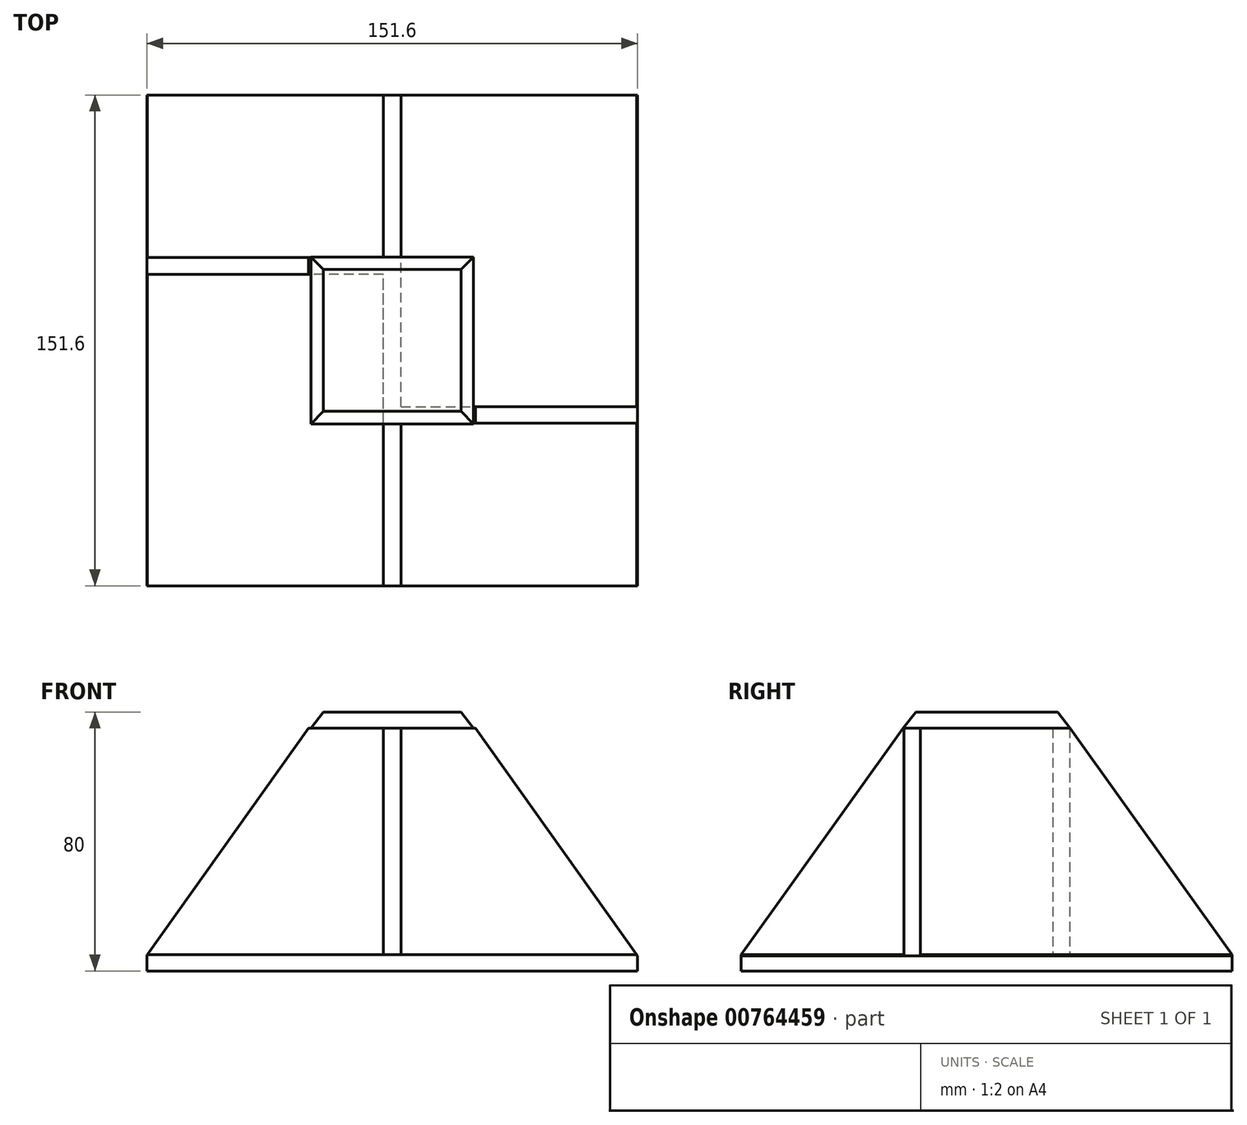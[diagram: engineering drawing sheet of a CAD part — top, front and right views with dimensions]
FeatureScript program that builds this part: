
annotation { "Feature Type Name" : "Feature", "Feature Type Description" : "" }
export const myFeature = defineFeature(function(context is Context, id is Id, definition is map)
    precondition{}
    {
        {
            var Q0;
            Q0=qCreatedBy(makeId("Top.planeOp"),FACE);
            var sketch = newSketch(context, id + "F0", { "sketchPlane" : qUnion([Q0])});
            skLineSegment(sketch, "E0.bottom", {"start": v(-75.8, 75.8) * mm, "end": v(75.8, 75.8) * mm});
            skLineSegment(sketch, "E0.top", {"start": v(-75.8, -75.8) * mm, "end": v(75.8, -75.8) * mm});
            skLineSegment(sketch, "E0.left", {"start": v(-75.8, 75.8) * mm, "end": v(-75.8, -75.8) * mm});
            skLineSegment(sketch, "E0.right", {"start": v(75.8, 75.8) * mm, "end": v(75.8, -75.8) * mm});
            skPoint(sketch, "E0.middle", {"position": v(0, 0) * mm});
            skSolve(sketch);
        }
        {
            var Q0;
            Q0 = qSketchRegion(id + "F0", true);
            extrude(context, id + "F1", {"entities" : qUnion([Q0]), "depth" : 5 * mm, "offsetDistance" : 25 * mm});
        }
        {
            var Q0;
            Q0=makeQuery(id+"F1.opExtrude","CAP_FACE",FACE,{"disambiguationData":[OSD([sQuery(id+"F0.wireOp",EDGE,"E0.bottom"),sQuery(id+"F0.wireOp",EDGE,"E0.top"),sQuery(id+"F0.wireOp",EDGE,"E0.left"),sQuery(id+"F0.wireOp",EDGE,"E0.right")])],"isStart":false});
            var sketch = newSketch(context, id + "F2", { "sketchPlane" : qUnion([Q0])});
            skLineSegment(sketch, "E1.bottom", {"start": v(2.72, -75.8) * mm, "end": v(-2.72, -75.8) * mm});
            skLineSegment(sketch, "E1.top", {"start": v(2.72, 75.8) * mm, "end": v(-2.72, 75.8) * mm});
            skLineSegment(sketch, "E1.left", {"start": v(2.72, -75.8) * mm, "end": v(2.72, 75.8) * mm});
            skLineSegment(sketch, "E1.right", {"start": v(-2.72, -75.8) * mm, "end": v(-2.72, 75.8) * mm});
            skPoint(sketch, "E1.middle", {"position": v(0, 0) * mm});
            skSolve(sketch);
        }
        {
            var Q0;
            Q0=makeQuery(id+"F2.imprint","IMPRINT",FACE,{"disambiguationData":[TD([[makeQuery(id+"F2.imprint","IMPRINT",EDGE,{"derivedFrom":sQuery(id+"F2.wireOp",EDGE,"E1.bottom")}),1.0]])]});
            extrude(context, id + "F3", {"entities" : qUnion([Q0]), "operationType" : NewBodyOperationType.ADD, "depth" : 70 * mm, "offsetDistance" : 25 * mm});
        }
        {
            var Q0;
            Q0=makeQuery(id+"F3.opExtrude","CAP_EDGE",EDGE,{"disambiguationData":[OSD([sQuery(id+"F2.wireOp",EDGE,"E1.bottom")])],"isStart":false});
            chamfer(context, id + "F4", {"entities" : qUnion([Q0]), "chamferType" : ChamferType.TWO_OFFSETS, "width1" : 50 * mm, "oppositeDirection" : false, "width2" : 70 * mm, "tangentPropagation" : true});
        }
        {
            var Q0;
            Q0=makeQuery(id+"F3.opExtrude","CAP_EDGE",EDGE,{"disambiguationData":[OSD([sQuery(id+"F2.wireOp",EDGE,"E1.top")])],"isStart":false});
            chamfer(context, id + "F5", {"entities" : qUnion([Q0]), "chamferType" : ChamferType.TWO_OFFSETS, "width1" : 70 * mm, "oppositeDirection" : false, "width2" : 50 * mm, "tangentPropagation" : true});
        }
        {
            var Q0;
            Q0=makeQuery(id+"F3.opExtrude","CAP_FACE",FACE,{"disambiguationData":[OSD([sQuery(id+"F2.wireOp",EDGE,"E1.bottom"),sQuery(id+"F2.wireOp",EDGE,"E1.top"),sQuery(id+"F2.wireOp",EDGE,"E1.left"),sQuery(id+"F2.wireOp",EDGE,"E1.right")])],"isStart":false});
            var sketch = newSketch(context, id + "F6", { "sketchPlane" : qUnion([Q0])});
            skLineSegment(sketch, "E2.bottom", {"start": v(25.1, -25.76) * mm, "end": v(-25.1, -25.76) * mm});
            skLineSegment(sketch, "E2.top", {"start": v(25.1, 25.76) * mm, "end": v(-25.1, 25.76) * mm});
            skLineSegment(sketch, "E2.left", {"start": v(25.1, -25.76) * mm, "end": v(25.1, 25.76) * mm});
            skLineSegment(sketch, "E2.right", {"start": v(-25.1, -25.76) * mm, "end": v(-25.1, 25.76) * mm});
            skPoint(sketch, "E2.middle", {"position": v(0, 0) * mm});
            skSolve(sketch);
        }
        {
            var Q0;
            Q0 = qSketchRegion(id + "F6", true);
            extrude(context, id + "F7", {"entities" : qUnion([Q0]), "operationType" : NewBodyOperationType.ADD, "depth" : 5 * mm, "offsetDistance" : 25 * mm});
        }
        {
            var Q0;
            Q0=makeQuery(id+"F7.opExtrude","CAP_EDGE",EDGE,{"disambiguationData":[OSD([sQuery(id+"F6.wireOp",EDGE,"E2.left")])],"isStart":false});
            var Q1;
            Q1=makeQuery(id+"F7.opExtrude","CAP_EDGE",EDGE,{"disambiguationData":[OSD([sQuery(id+"F6.wireOp",EDGE,"E2.bottom")])],"isStart":false});
            var Q2;
            Q2=makeQuery(id+"F7.opExtrude","CAP_EDGE",EDGE,{"disambiguationData":[OSD([sQuery(id+"F6.wireOp",EDGE,"E2.top")])],"isStart":false});
            var Q3;
            Q3=makeQuery(id+"F7.opExtrude","CAP_EDGE",EDGE,{"disambiguationData":[OSD([sQuery(id+"F6.wireOp",EDGE,"E2.right")])],"isStart":false});
            chamfer(context, id + "F8", {"entities" : qUnion([Q0, Q1, Q2, Q3]), "chamferType" : ChamferType.TWO_OFFSETS, "width1" : 3.85 * mm, "oppositeDirection" : false, "width2" : 5 * mm, "tangentPropagation" : true});
        }
        {
            var Q0;
            {var subQ0=sQuery(id+"F0.wireOp",EDGE,"E0.left");var subQ1=sQuery(id+"F0.wireOp",EDGE,"E0.top");var subQ2=sQuery(id+"F0.wireOp",EDGE,"E0.bottom");Q0=makeQuery(id+"F3.boolean.opBoolean","SPLIT",FACE,{"disambiguationData":[TD([makeQuery(id+"F1.opExtrude","SWEPT_FACE",FACE,{"disambiguationData":[OSD([subQ0])]})])],"derivedFrom":makeQuery(id+"F1.opExtrude","CAP_FACE",FACE,{"disambiguationData":[OSD([subQ2,subQ1,subQ0,sQuery(id+"F0.wireOp",EDGE,"E0.right")])],"isStart":false})});}
            var sketch = newSketch(context, id + "F9", { "sketchPlane" : qUnion([Q0])});
            skLineSegment(sketch, "E3.bottom", {"start": v(-2.72, 25.66) * mm, "end": v(-75.8, 25.66) * mm});
            skLineSegment(sketch, "E3.top", {"start": v(-2.72, 20.46) * mm, "end": v(-75.8, 20.46) * mm});
            skLineSegment(sketch, "E3.left", {"start": v(-2.72, 25.66) * mm, "end": v(-2.72, 20.46) * mm});
            skLineSegment(sketch, "E3.right", {"start": v(-75.8, 25.66) * mm, "end": v(-75.8, 20.46) * mm});
            skSolve(sketch);
        }
        {
            var Q0;
            Q0 = qSketchRegion(id + "F9", true);
            extrude(context, id + "F10", {"entities" : qUnion([Q0]), "operationType" : NewBodyOperationType.ADD, "depth" : 70 * mm, "offsetDistance" : 25 * mm});
        }
        {
            var Q0;
            Q0=makeQuery(id+"F10.opExtrude","CAP_EDGE",EDGE,{"disambiguationData":[OSD([sQuery(id+"F9.wireOp",EDGE,"E3.right")])],"isStart":false});
            chamfer(context, id + "F11", {"entities" : qUnion([Q0]), "chamferType" : ChamferType.OFFSET_ANGLE, "width" : 50 * mm, "oppositeDirection" : false, "angle" : 54.6 * degree, "tangentPropagation" : true});
        }
        {
            var Q0;
            {var subQ0=sQuery(id+"F0.wireOp",EDGE,"E0.top");var subQ1=sQuery(id+"F0.wireOp",EDGE,"E0.right");var subQ2=sQuery(id+"F0.wireOp",EDGE,"E0.bottom");Q0=makeQuery(id+"F3.boolean.opBoolean","SPLIT",FACE,{"disambiguationData":[TD([makeQuery(id+"F1.opExtrude","SWEPT_FACE",FACE,{"disambiguationData":[OSD([subQ1])]})])],"derivedFrom":makeQuery(id+"F1.opExtrude","CAP_FACE",FACE,{"disambiguationData":[OSD([subQ2,subQ0,sQuery(id+"F0.wireOp",EDGE,"E0.left"),subQ1])],"isStart":false})});}
            var sketch = newSketch(context, id + "F12", { "sketchPlane" : qUnion([Q0])});
            skLineSegment(sketch, "E4.bottom", {"start": v(2.72, -25.53) * mm, "end": v(75.8, -25.53) * mm});
            skLineSegment(sketch, "E4.top", {"start": v(2.72, -20.45) * mm, "end": v(75.8, -20.45) * mm});
            skLineSegment(sketch, "E4.left", {"start": v(2.72, -25.53) * mm, "end": v(2.72, -20.45) * mm});
            skLineSegment(sketch, "E4.right", {"start": v(75.8, -25.53) * mm, "end": v(75.8, -20.45) * mm});
            skSolve(sketch);
        }
        {
            var Q0;
            Q0 = qSketchRegion(id + "F12", true);
            extrude(context, id + "F13", {"entities" : qUnion([Q0]), "operationType" : NewBodyOperationType.ADD, "depth" : 70 * mm, "offsetDistance" : 25 * mm});
        }
        {
            var Q0;
            Q0=makeQuery(id+"F13.opExtrude","CAP_EDGE",EDGE,{"disambiguationData":[OSD([sQuery(id+"F12.wireOp",EDGE,"E4.right")])],"isStart":false});
            chamfer(context, id + "F14", {"entities" : qUnion([Q0]), "chamferType" : ChamferType.OFFSET_ANGLE, "width" : 50 * mm, "oppositeDirection" : true, "angle" : 54.6 * degree, "tangentPropagation" : true});
        }
    });
